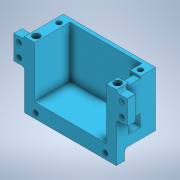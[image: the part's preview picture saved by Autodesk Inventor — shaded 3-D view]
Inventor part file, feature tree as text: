
AUTODESK INVENTOR PART (.ipt)
format: ipt  version: 2022 (Build 260153000, 153)  size: 518,144 bytes
history: native  units: mm
features: sketch x17, extrude x16, fillet x9, other x4, projected_geometry x4, mirror x1
ambient origin geometry x8: Origin, YZ Plane, XZ Plane, XY Plane, X Axis, Y Axis, Z Axis, Center Point
bodies: Body1 (feature_tree)
feature tree (51):
  other  "Твердое тело1"
  extrude  "Выдавливание1"  Depth=29.5mm
  extrude  "Выдавливание2"  Depth=60.0mm
  extrude  "Выдавливание3"  Depth=3.0mm
  other  "РабПлоскость1"
  other  "РабПлоскость2"
  extrude  "Выдавливание8"  Depth=43.0mm TaperAngle=0.0deg
  extrude  "Выдавливание9"  Depth=3.0mm TaperAngle=0.0deg
  extrude  "Выдавливание10"  Depth=4.2mm
  extrude  "Выдавливание13"  Depth=30.0mm TaperAngle=0.0deg
  other  "РабПлоскость6"
  mirror  "Зеркальное отражение5"
  extrude  "Выдавливание14"  [1 undecoded]
  extrude  "Выдавливание15"  Depth=8.3mm
  extrude  "Выдавливание16"  Depth=9.0mm
  fillet  "Сопряжение18"  Radius=9.0mm
  fillet  "Сопряжение19"  Radius=4.2mm
  fillet  "Сопряжение20"  Radius=7.0mm
  extrude  "Выдавливание17"  Depth=7.15mm
  extrude  "Выдавливание18"  Depth=3.0mm TaperAngle=0.0deg
  extrude  "Выдавливание20"  Depth=0.2mm
  extrude  "Выдавливание21"  Depth=0.2mm
  extrude  "Выдавливание22"  Depth=7.0mm TaperAngle=0.0deg
  extrude  "Выдавливание23"  Depth=0.2mm
  fillet  "Сопряжение16"  Radius=19.0mm
  fillet  "Сопряжение10"  Radius=68.0mm
  fillet  "Сопряжение6"  Radius=2.0mm
  fillet  "Сопряжение7"  Radius=10.0mm
  fillet  "Сопряжение14"  Radius=77.0mm
  fillet  "Сопряжение15"  Radius=5.0mm
  sketch  "Эскиз14"
  sketch  "Эскиз1"
  sketch  "Эскиз2"
  sketch  "Эскиз3"
  sketch  "Эскиз8"
  sketch  "Эскиз9"
  sketch  "Эскиз10"
  sketch  "Эскиз15"
  sketch  "Эскиз17"
  projected_geometry  "Спроецированная петля1"
  sketch  "Эскиз18"
  projected_geometry  "Спроецированная петля2"
  sketch  "Эскиз19"
  projected_geometry  "Спроецированная петля3"
  sketch  "Эскиз20"
  sketch  "Эскиз21"
  sketch  "Эскиз23"
  sketch  "Эскиз24"
  sketch  "Эскиз25"
  sketch  "Эскиз26"
  projected_geometry  "Спроецированная петля4"
note: 1 required parameter value undecoded (feature->parameter linkage not recoverable at this tier; creation-order binding heuristic only, values carry confidence <= 0.55)
